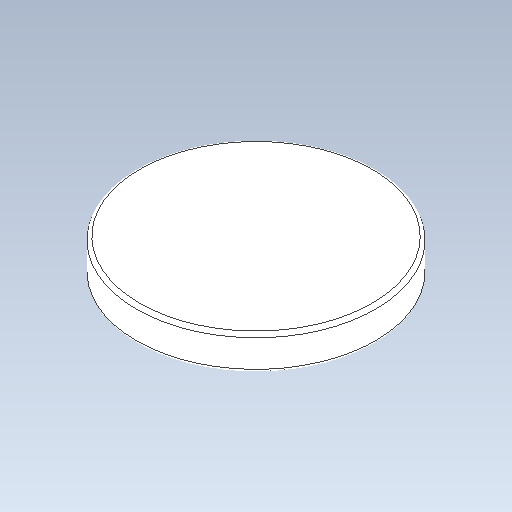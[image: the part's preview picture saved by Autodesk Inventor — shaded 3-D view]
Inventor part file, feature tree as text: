
AUTODESK INVENTOR PART (.ipt)
format: ipt  version: 2021.2 (Build 252289000, 289)  size: 100,864 bytes
history: native  units: in
note: dims shown in document units (in); Inventor stores cm internally (conversion verified against a paired STEP export)
features: fillet x1
ambient origin geometry x8: Origin, YZ Plane, XZ Plane, XY Plane, X Axis, Y Axis, Z Axis, Center Point
bodies: Solid1 (feature_tree)
feature tree (1):
  fillet  "Fillet1"  [1 undecoded]
note: 1 required parameter value undecoded (feature->parameter linkage not recoverable at this tier; creation-order binding heuristic only, values carry confidence <= 0.55)
